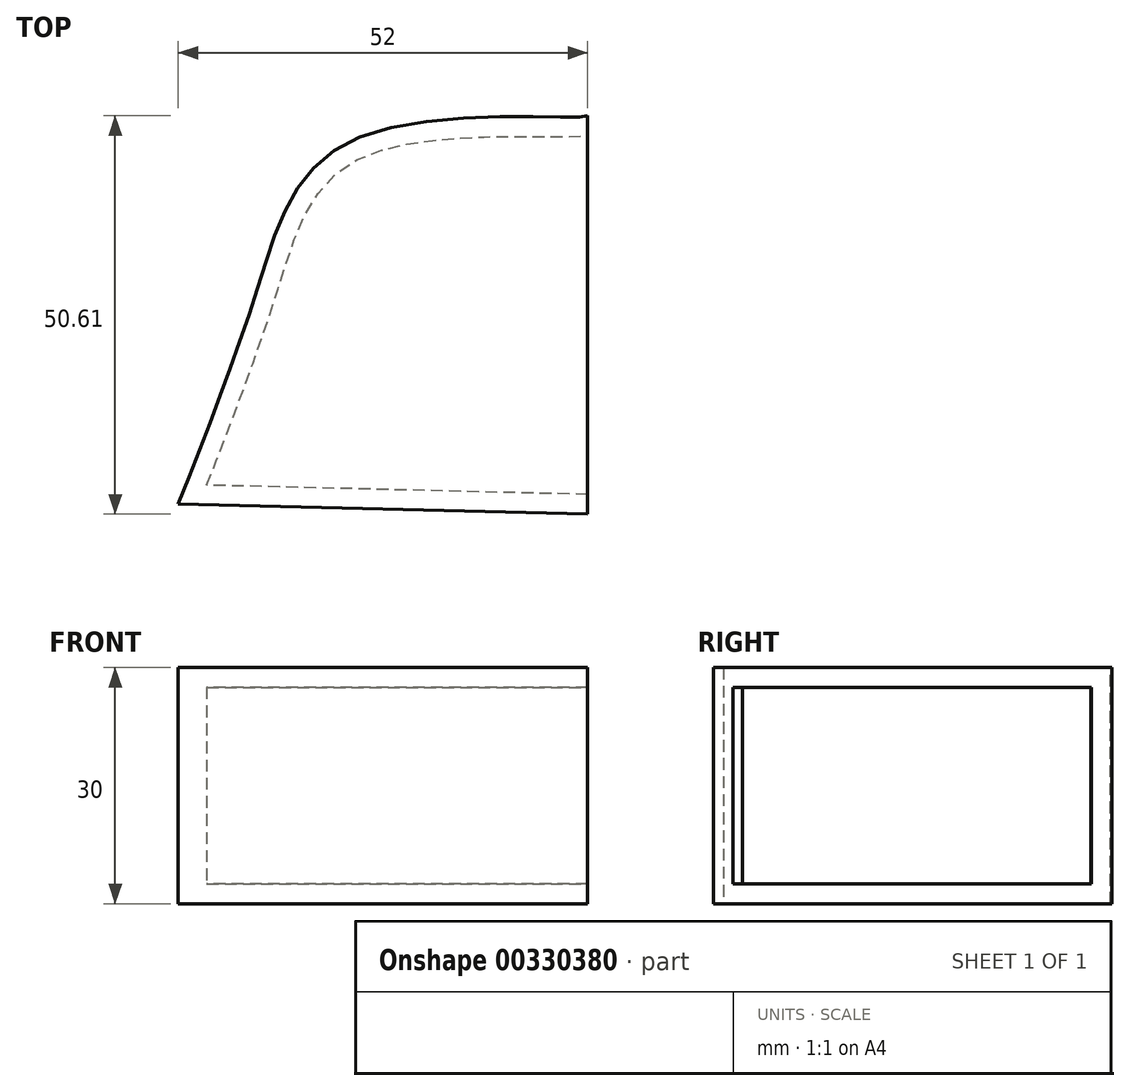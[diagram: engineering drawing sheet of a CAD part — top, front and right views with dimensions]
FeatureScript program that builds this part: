
annotation { "Feature Type Name" : "Feature", "Feature Type Description" : "" }
export const myFeature = defineFeature(function(context is Context, id is Id, definition is map)
    precondition{}
    {
        {
            var Q0;
            Q0=qCreatedBy(makeId("Top.planeOp"),FACE);
            var sketch = newSketch(context, id + "F0", { "sketchPlane" : qUnion([Q0])});
            skFitSpline(sketch, "E0", {"points": [v(-52.9, 10.77) * mm, v(-42.88, 38.03) * mm, v(-29.48, 57.57) * mm, v(-0.9, 60.12) * mm, v(-1.77, 60.69) * mm], "startDerivative": vector(33.24, 84.52) * mm, "endDerivative": vector(-24.45, 10.85) * mm});
            skLineSegment(sketch, "E1", {"start": v(-0.9, 60.12) * mm, "end": v(-0.9, 9.5) * mm});
            skLineSegment(sketch, "E2", {"start": v(-0.9, 9.5) * mm, "end": v(-52.9, 10.77) * mm});
            skSolve(sketch);
        }
        {
            var Q0;
            Q0 = qSketchRegion(id + "F0", true);
            var Q1;
            {var subQ2=sQuery(id+"F0.wireOp",EDGE,"E1");Q1=makeQuery(id+"F0.imprint","IMPRINT",FACE,{"disambiguationData":[TD([[makeQuery(id+"F0.imprint","IMPRINT",EDGE,{"derivedFrom":subQ2}),-1.0]])]});}
            extrude(context, id + "F1", {"entities" : qUnion([Q0, Q1]), "depth" : 30 * mm});
        }
        {
            var Q0;
            Q0=makeQuery(id+"F1.opExtrude","SWEPT_FACE",FACE,{"disambiguationData":[OSD([sQuery(id+"F0.wireOp",EDGE,"E1")])]});
            shell(context, id + "F2", {"entities" : qUnion([Q0]), "thickness" : 2.5 * mm});
        }
    });
